FCSTD DOCUMENT  (FreeCAD 0.20R0.20)
Label: 008
License: All rights reserved
LicenseURL: http://en.wikipedia.org/wiki/All_rights_reserved
objects: Sketcher::SketchObject×1
note: 1 computed .brp shape members not serialized (recipe doc carries the construction recipe); baked Part::Feature solids carry a one-line shape summary decoded from their .brp

FEATURE [Sketcher::SketchObject] Sketch  label="baseL"
  FullyConstrained = true
  sketch-geometry (30):
    g0: LineSegment StartX=0 StartY=0 StartZ=0 EndX=0 EndY=200 EndZ=0
    g1: LineSegment StartX=390 StartY=200 StartZ=0 EndX=390 EndY=0 EndZ=0
    g2: LineSegment StartX=0 StartY=200 StartZ=0 EndX=190 EndY=200 EndZ=0
    g3: LineSegment StartX=0 StartY=0 StartZ=0 EndX=190 EndY=0 EndZ=0
    g4: LineSegment StartX=390 StartY=200 StartZ=0 EndX=200 EndY=200 EndZ=0
    g5: LineSegment StartX=390 StartY=0 StartZ=0 EndX=200 EndY=0 EndZ=0
    g6: LineSegment StartX=190 StartY=0 StartZ=0 EndX=190 EndY=14 EndZ=0
    g7: LineSegment StartX=200 StartY=0 StartZ=0 EndX=200 EndY=14 EndZ=0
    g8: LineSegment StartX=200 StartY=200 StartZ=0 EndX=200 EndY=186 EndZ=0
    g9: LineSegment StartX=24 StartY=186 StartZ=0 EndX=190 EndY=105.929 EndZ=0
    g10: LineSegment StartX=16 StartY=178 StartZ=0 EndX=177.707 EndY=100 EndZ=0
    g11: LineSegment StartX=16 StartY=22 StartZ=0 EndX=177.707 EndY=100 EndZ=0
    g12: LineSegment StartX=24 StartY=14 StartZ=0 EndX=190 EndY=94.0706 EndZ=0
    g13: LineSegment StartX=16 StartY=22 StartZ=0 EndX=16 EndY=178 EndZ=0
    g14: LineSegment StartX=212.293 StartY=100 StartZ=0 EndX=374 EndY=22 EndZ=0
    g15: LineSegment StartX=200 StartY=94.0706 StartZ=0 EndX=366 EndY=14 EndZ=0
    g16: LineSegment StartX=374 StartY=178 StartZ=0 EndX=212.293 EndY=100 EndZ=0
    g17: LineSegment StartX=200 StartY=105.929 StartZ=0 EndX=366 EndY=186 EndZ=0
    g18: LineSegment StartX=212.293 StartY=100 StartZ=0 EndX=200 EndY=100 EndZ=0
    g19: LineSegment StartX=374 StartY=178 StartZ=0 EndX=374 EndY=22 EndZ=0
    g20: LineSegment StartX=366 StartY=14 StartZ=0 EndX=200 EndY=14 EndZ=0
    g21: LineSegment StartX=200 StartY=186 StartZ=0 EndX=366 EndY=186 EndZ=0
    g22: LineSegment StartX=24 StartY=14 StartZ=0 EndX=190 EndY=14 EndZ=0
    g23: LineSegment StartX=190 StartY=186 StartZ=0 EndX=24 EndY=186 EndZ=0
    g24: LineSegment StartX=177.707 StartY=100 StartZ=0 EndX=190 EndY=100 EndZ=0
    g25: Circle CenterX=190 CenterY=100 CenterZ=0 NormalX=0 NormalY=0 NormalZ=1 AngleXU=0 Radius=22.2927
    g26: Circle CenterX=190 CenterY=100 CenterZ=0 NormalX=0 NormalY=0 NormalZ=1 AngleXU=0 Radius=11.6257
    g27: LineSegment StartX=190 StartY=94.0706 StartZ=0 EndX=190.27 EndY=94.2009 EndZ=0
    g28: Circle CenterX=200 CenterY=100 CenterZ=0 NormalX=0 NormalY=0 NormalZ=1 AngleXU=0 Radius=11.3269
    g29: Circle CenterX=200 CenterY=100 CenterZ=0 NormalX=0 NormalY=0 NormalZ=1 AngleXU=0 Radius=22.2927
  constraints (74):
    c: Coincident(g0,g-1)
    c: Vertical(g0)
    c: Distance(g0) = 200
    c: Vertical(g1)
    c: Distance(g1) = 200
    c: Coincident(g2,g0)
    c: Horizontal(g2)
    c: Distance(g2) = 190
    c: Coincident(g3,g0)
    c: Horizontal(g3)
    c: Distance(g3) = 190
    c: Block(g1)
    c: Coincident(g4,g1)
    c: Horizontal(g4)
    c: Coincident(g5,g1)
    c: Horizontal(g5)
    c: Distance(g5) = 190
    c: Distance(g4) = 190
    c: Coincident(g6,g3)
    c: Vertical(g6)
    c: Coincident(g7,g5)
    c: Vertical(g7)
    c: Coincident(g8,g4)
    c: Vertical(g8)
    c: Distance(g8) = 14
    c: Distance(g6) = 14
    c: Distance(g7) = 14
    c: Block(g9)
    c: Block(g10)
    c: PointOnObject(g12,g10)
    c: Block(g12)
    c: Block(g11)
    c: Coincident(g11,g10)
    c: Vertical(g13)
    c: Block(g13)
    c: Block(g17)
    c: Block(g16)
    c: Block(g14)
    c: Block(g15)
    c: PointOnObject(g17,g14)
    c: PointOnObject(g15,g16)
    c: Coincident(g14,g16)
    c: Coincident(g18,g14)
    c: Horizontal(g18)
    c: Block(g18)
    c: Coincident(g19,g16)
    c: Coincident(g19,g14)
    c: Vertical(g19)
    c: Coincident(g20,g15)
    c: Coincident(g20,g7)
    c: Horizontal(g20)
    c: Coincident(g21,g8)
    c: Coincident(g21,g17)
    c: Horizontal(g21)
    c: Coincident(g22,g12)
    c: Coincident(g22,g6)
    c: Horizontal(g22)
    c: Coincident(g23,g9)
    c: Horizontal(g23)
    c: Coincident(g24,g10)
    c: Horizontal(g24)
    c: Block(g24)
    c: Coincident(g25,g24)
    c: PointOnObject(g14,g25)
    c: Coincident(g26,g24)
    c: PointOnObject(g15,g26)
    c: Coincident(g27,g12)
    c: Angle(g12,g27) = 3.14159
    c: Distance(g27) = 0.3
    c: Coincident(g28,g18)
    c: PointOnObject(g27,g28)
    c: Coincident(g29,g18)
    c: PointOnObject(g10,g29)
    c: Block(g23)
